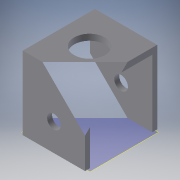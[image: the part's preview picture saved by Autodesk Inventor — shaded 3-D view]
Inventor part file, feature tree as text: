
AUTODESK INVENTOR PART (.ipt)
format: ipt  version: 2016 (Build 200138000, 138)  size: 121,344 bytes
history: native  units: in
note: dims shown in document units (in); Inventor stores cm internally (conversion verified against a paired STEP export)
features: sketch x5, extrude x4, reference x2, plane x1
ambient origin geometry x8: Origin, YZ Plane, XZ Plane, XY Plane, X Axis, Y Axis, Z Axis, Center Point
bodies: Solid1 (feature_tree)
feature tree (12):
  plane  "Work Plane1"
  extrude  "Extrusion1"  Depth=0.6875in TaperAngle=0.0deg
  extrude  "Extrusion2"  Depth=0.0625in TaperAngle=0.0deg
  extrude  "Extrusion3"  [1 undecoded]
  sketch  "Sketch5"
  extrude  "Extrusion5"  [1 undecoded]
  sketch  "Sketch1"  dims[d0=0.6875in d1=0.0in d2=1.0in d3=0.0in]
  reference  "Reference1"
  sketch  "Sketch2"  dims[d4=0.0625in d5=0.0in d8=0.0625in d9=0.0in]
  sketch  "Sketch3"
  sketch  "Sketch6"
  reference  "Reference4"
note: 2 required parameter values undecoded (feature->parameter linkage not recoverable at this tier; creation-order binding heuristic only, values carry confidence <= 0.55)
